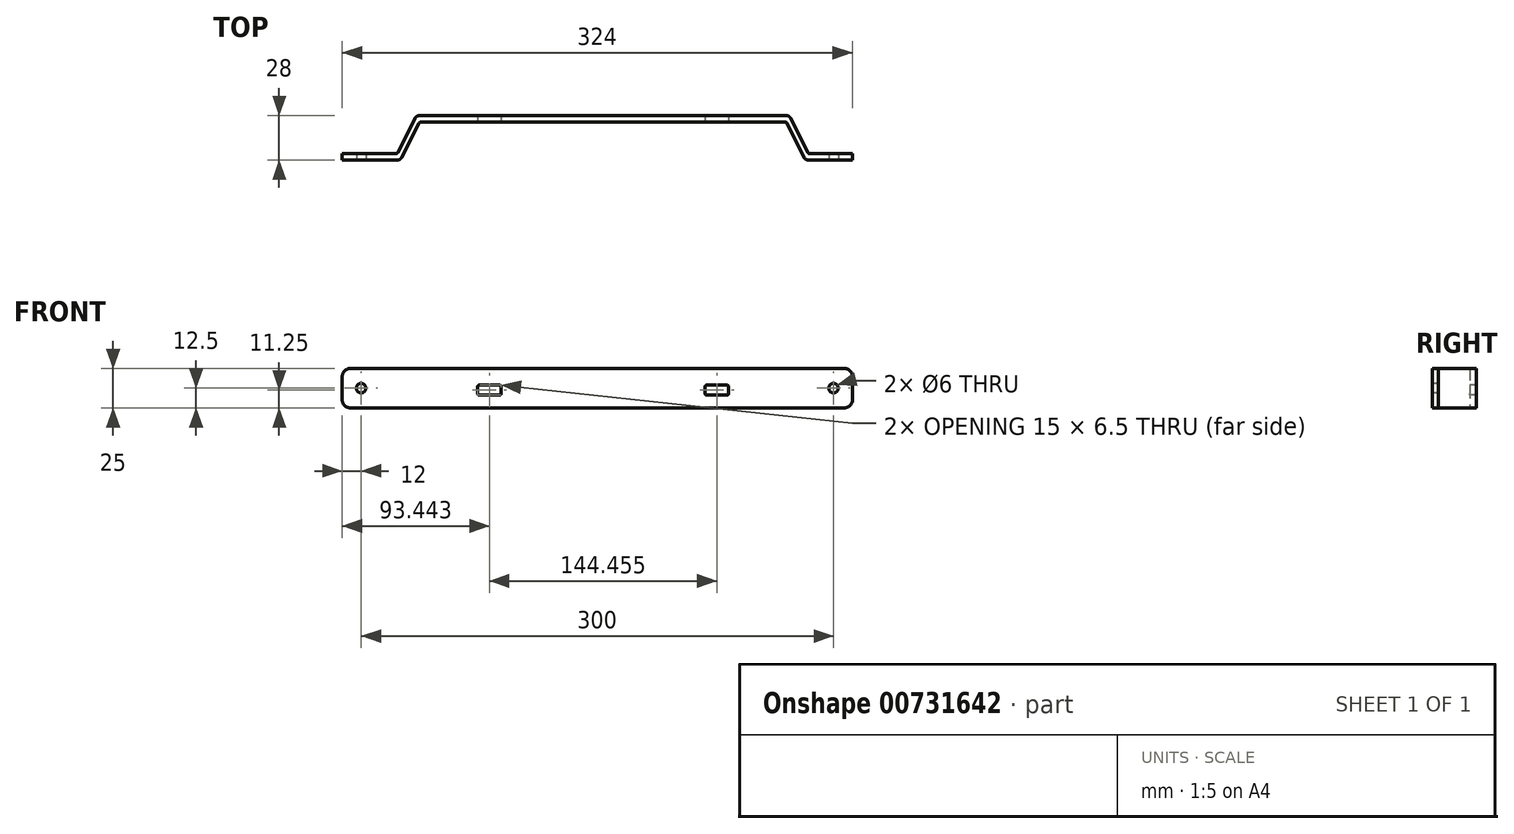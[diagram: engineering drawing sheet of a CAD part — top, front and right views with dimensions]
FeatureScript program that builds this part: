
annotation { "Feature Type Name" : "Feature", "Feature Type Description" : "" }
export const myFeature = defineFeature(function(context is Context, id is Id, definition is map)
    precondition{}
    {
        {
            var Q0;
            Q0=qCreatedBy(makeId("Top.planeOp"),FACE);
            var sketch = newSketch(context, id + "F0", { "sketchPlane" : qUnion([Q0])});
            skLineSegment(sketch, "E0.bottom", {"start": v(0, 0) * mm, "end": v(34.23, 0) * mm});
            skLineSegment(sketch, "E0.top", {"start": v(0, -4) * mm, "end": v(35.46, -4) * mm});
            skLineSegment(sketch, "E0.left", {"start": v(0, 0) * mm, "end": v(0, -4) * mm});
            skLineSegment(sketch, "E1.bottom", {"start": v(48.55, 24) * mm, "end": v(282.45, 24) * mm});
            skLineSegment(sketch, "E1.top", {"start": v(49.94, 20) * mm, "end": v(281.4, 20) * mm});
            skLineSegment(sketch, "E2.bottom", {"start": v(296.77, 0) * mm, "end": v(324, 0) * mm});
            skLineSegment(sketch, "E2.top", {"start": v(295.56, -4) * mm, "end": v(324, -4) * mm});
            skLineSegment(sketch, "E2.right", {"start": v(324, 0) * mm, "end": v(324, -4) * mm});
            skLineSegment(sketch, "E3", {"start": v(46.3, 22.62) * mm, "end": v(35.35, 0.7) * mm});
            skLineSegment(sketch, "E4", {"start": v(48.83, 19.32) * mm, "end": v(37.7, -2.63) * mm});
            skLineSegment(sketch, "E5", {"start": v(293.31, -2.6) * mm, "end": v(282.52, 19.3) * mm});
            skLineSegment(sketch, "E6", {"start": v(295.65, 0.7) * mm, "end": v(284.7, 22.62) * mm});
            skPoint(sketch, "E7.visualSharp", {"position": v(282.18, 20) * mm});
            skArc(sketch, "E7.filletArc", {"start": v(282.52, 19.3) * mm, "mid": v(282.06, 19.81) * mm, "end": v(281.4, 20) * mm});
            skPoint(sketch, "E8.visualSharp", {"position": v(296, 0) * mm});
            skArc(sketch, "E8.filletArc", {"start": v(295.65, 0.7) * mm, "mid": v(296.12, 0.19) * mm, "end": v(296.77, 0) * mm});
            skPoint(sketch, "E9.visualSharp", {"position": v(49.18, 20) * mm});
            skArc(sketch, "E9.filletArc", {"start": v(49.94, 20) * mm, "mid": v(49.29, 19.82) * mm, "end": v(48.83, 19.32) * mm});
            skPoint(sketch, "E10.visualSharp", {"position": v(35, 0) * mm});
            skArc(sketch, "E10.filletArc", {"start": v(34.23, 0) * mm, "mid": v(34.88, 0.19) * mm, "end": v(35.35, 0.7) * mm});
            skPoint(sketch, "E11.visualSharp", {"position": v(37, -4) * mm});
            skArc(sketch, "E11.filletArc", {"start": v(35.46, -4) * mm, "mid": v(36.77, -3.63) * mm, "end": v(37.7, -2.63) * mm});
            skPoint(sketch, "E12.visualSharp", {"position": v(47, 24) * mm});
            skArc(sketch, "E12.filletArc", {"start": v(48.55, 24) * mm, "mid": v(47.23, 23.63) * mm, "end": v(46.3, 22.62) * mm});
            skPoint(sketch, "E13.visualSharp", {"position": v(294, -4) * mm});
            skArc(sketch, "E13.filletArc", {"start": v(293.31, -2.6) * mm, "mid": v(294.23, -3.62) * mm, "end": v(295.56, -4) * mm});
            skPoint(sketch, "E14.visualSharp", {"position": v(284, 24) * mm});
            skArc(sketch, "E14.filletArc", {"start": v(284.7, 22.62) * mm, "mid": v(283.77, 23.63) * mm, "end": v(282.45, 24) * mm});
            skSolve(sketch);
        }
        {
            var Q0;
            Q0 = qSketchRegion(id + "F0", true);
            extrude(context, id + "F1", {"entities" : qUnion([Q0]), "depth" : 25 * mm, "offsetDistance" : 25 * mm});
        }
        {
            var Q0;
            Q0=makeQuery(id+"F1.opExtrude","SWEPT_FACE",FACE,{"disambiguationData":[OSD([sQuery(id+"F0.wireOp",EDGE,"E1.top")])]});
            var sketch = newSketch(context, id + "F2", { "sketchPlane" : qUnion([Q0])});
            skLineSegment(sketch, "E15.bottom", {"start": v(87.2, 14.5) * mm, "end": v(99.7, 14.5) * mm});
            skLineSegment(sketch, "E15.top", {"start": v(87.2, 8) * mm, "end": v(99.7, 8) * mm});
            skLineSegment(sketch, "E15.left", {"start": v(85.94, 13.25) * mm, "end": v(85.94, 9.25) * mm});
            skLineSegment(sketch, "E15.right", {"start": v(100.94, 13.25) * mm, "end": v(100.94, 9.25) * mm});
            skLineSegment(sketch, "E16.bottom", {"start": v(231.65, 14.5) * mm, "end": v(244.15, 14.5) * mm});
            skLineSegment(sketch, "E16.top", {"start": v(231.65, 8) * mm, "end": v(244.15, 8) * mm});
            skLineSegment(sketch, "E16.left", {"start": v(230.4, 13.25) * mm, "end": v(230.4, 9.25) * mm});
            skLineSegment(sketch, "E16.right", {"start": v(245.4, 13.25) * mm, "end": v(245.4, 9.25) * mm});
            skPoint(sketch, "E17.visualSharp", {"position": v(245.4, 14.5) * mm});
            skArc(sketch, "E17.filletArc", {"start": v(245.4, 13.25) * mm, "mid": v(245.03, 14.13) * mm, "end": v(244.15, 14.5) * mm});
            skPoint(sketch, "E18.visualSharp", {"position": v(245.4, 8) * mm});
            skArc(sketch, "E18.filletArc", {"start": v(244.15, 8) * mm, "mid": v(245.03, 8.37) * mm, "end": v(245.4, 9.25) * mm});
            skPoint(sketch, "E19.visualSharp", {"position": v(230.4, 8) * mm});
            skArc(sketch, "E19.filletArc", {"start": v(230.4, 9.25) * mm, "mid": v(230.76, 8.37) * mm, "end": v(231.65, 8) * mm});
            skPoint(sketch, "E20.visualSharp", {"position": v(230.4, 14.5) * mm});
            skArc(sketch, "E20.filletArc", {"start": v(231.65, 14.5) * mm, "mid": v(230.76, 14.13) * mm, "end": v(230.4, 13.25) * mm});
            skPoint(sketch, "E21.visualSharp", {"position": v(85.94, 14.5) * mm});
            skArc(sketch, "E21.filletArc", {"start": v(87.2, 14.5) * mm, "mid": v(86.3, 14.13) * mm, "end": v(85.94, 13.25) * mm});
            skPoint(sketch, "E22.visualSharp", {"position": v(85.94, 8) * mm});
            skArc(sketch, "E22.filletArc", {"start": v(85.94, 9.25) * mm, "mid": v(86.3, 8.37) * mm, "end": v(87.2, 8) * mm});
            skPoint(sketch, "E23.visualSharp", {"position": v(100.94, 14.5) * mm});
            skArc(sketch, "E23.filletArc", {"start": v(100.94, 13.25) * mm, "mid": v(100.58, 14.13) * mm, "end": v(99.7, 14.5) * mm});
            skPoint(sketch, "E24.visualSharp", {"position": v(100.94, 8) * mm});
            skArc(sketch, "E24.filletArc", {"start": v(99.7, 8) * mm, "mid": v(100.58, 8.37) * mm, "end": v(100.94, 9.25) * mm});
            skSolve(sketch);
        }
        {
            var Q0;
            Q0 = qSketchRegion(id + "F2", true);
            extrude(context, id + "F3", {"entities" : qUnion([Q0]), "operationType" : NewBodyOperationType.REMOVE, "oppositeDirection" : true, "depth" : 4 * mm, "offsetDistance" : 25 * mm});
        }
        {
            var Q0;
            Q0=makeQuery(id+"F1.opExtrude","CAP_EDGE",EDGE,{"disambiguationData":[OSD([sQuery(id+"F0.wireOp",EDGE,"E2.right")])],"isStart":false});
            var Q1;
            Q1=makeQuery(id+"F1.opExtrude","CAP_EDGE",EDGE,{"disambiguationData":[OSD([sQuery(id+"F0.wireOp",EDGE,"E2.right")])],"isStart":true});
            var Q2;
            Q2=makeQuery(id+"F1.opExtrude","CAP_EDGE",EDGE,{"disambiguationData":[OSD([sQuery(id+"F0.wireOp",EDGE,"E0.left")])],"isStart":false});
            var Q3;
            Q3=makeQuery(id+"F1.opExtrude","CAP_EDGE",EDGE,{"disambiguationData":[OSD([sQuery(id+"F0.wireOp",EDGE,"E0.left")])],"isStart":true});
            fillet(context, id + "F4", {"entities" : qUnion([Q0, Q1, Q2, Q3]), "radius" : 5 * mm, "tangentPropagation" : true, "allowEdgeOverflow" : false});
        }
        {
            var Q0;
            Q0=makeQuery(id+"F1.opExtrude","SWEPT_FACE",FACE,{"disambiguationData":[OSD([sQuery(id+"F0.wireOp",EDGE,"E0.top")])]});
            var sketch = newSketch(context, id + "F5", { "sketchPlane" : qUnion([Q0])});
            skCircle(sketch, "E25", {"center": v(12, 12.5) * mm, "radius": 3 * mm});
            skSolve(sketch);
        }
        {
            var Q0;
            Q0 = qSketchRegion(id + "F5", true);
            extrude(context, id + "F6", {"entities" : qUnion([Q0]), "operationType" : NewBodyOperationType.REMOVE, "oppositeDirection" : true, "depth" : 4 * mm, "offsetDistance" : 25 * mm});
        }
        {
            var Q0;
            Q0=makeQuery(id+"F1.opExtrude","SWEPT_FACE",FACE,{"disambiguationData":[OSD([sQuery(id+"F0.wireOp",EDGE,"E2.top")])]});
            var sketch = newSketch(context, id + "F7", { "sketchPlane" : qUnion([Q0])});
            skCircle(sketch, "E26", {"center": v(312, 12.5) * mm, "radius": 3 * mm});
            skSolve(sketch);
        }
        {
            var Q0;
            Q0 = qSketchRegion(id + "F7", true);
            extrude(context, id + "F8", {"entities" : qUnion([Q0]), "operationType" : NewBodyOperationType.REMOVE, "oppositeDirection" : true, "depth" : 4 * mm, "offsetDistance" : 25 * mm});
        }
    });
